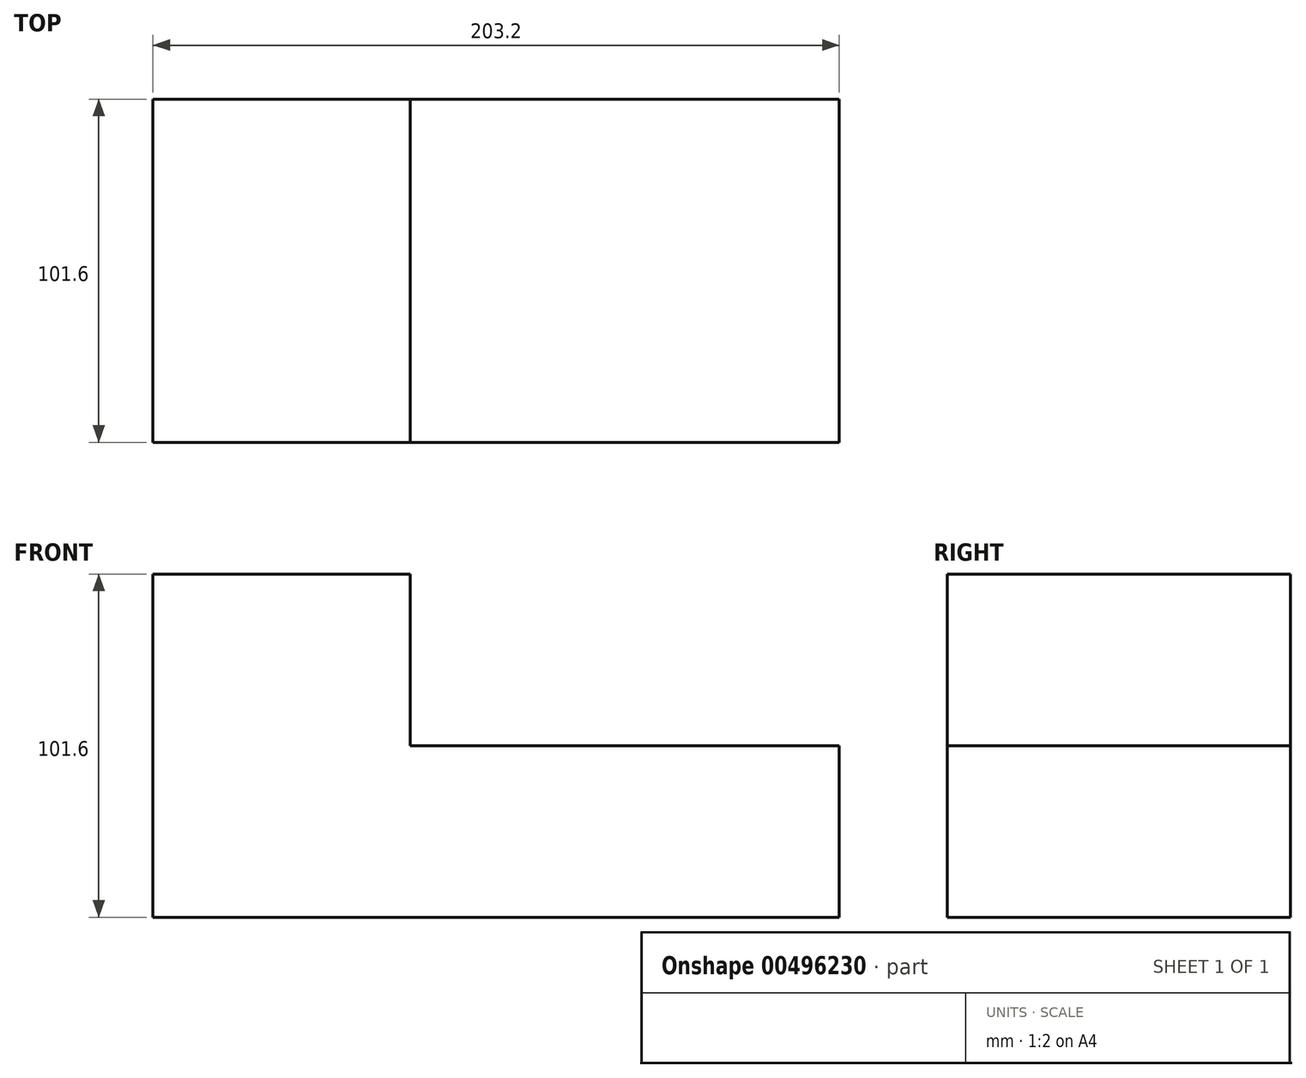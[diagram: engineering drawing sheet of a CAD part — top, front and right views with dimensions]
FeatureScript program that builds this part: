
annotation { "Feature Type Name" : "Feature", "Feature Type Description" : "" }
export const myFeature = defineFeature(function(context is Context, id is Id, definition is map)
    precondition{}
    {
        {
            var Q0;
            Q0=qCreatedBy(makeId("Front.planeOp"),FACE);
            var sketch = newSketch(context, id + "F0", { "sketchPlane" : qUnion([Q0])});
            skLineSegment(sketch, "E0.bottom", {"start": v(0, 0) * mm, "end": v(203.2, 0) * mm});
            skLineSegment(sketch, "E0.top", {"start": v(0, 101.6) * mm, "end": v(203.2, 101.6) * mm});
            skLineSegment(sketch, "E0.left", {"start": v(0, 0) * mm, "end": v(0, 101.6) * mm});
            skLineSegment(sketch, "E0.right", {"start": v(203.2, 0) * mm, "end": v(203.2, 101.6) * mm});
            skLineSegment(sketch, "E1.bottom", {"start": v(203.2, 101.6) * mm, "end": v(76.2, 101.6) * mm});
            skLineSegment(sketch, "E1.top", {"start": v(203.2, 50.8) * mm, "end": v(76.2, 50.8) * mm});
            skLineSegment(sketch, "E1.left", {"start": v(203.2, 101.6) * mm, "end": v(203.2, 50.8) * mm});
            skLineSegment(sketch, "E1.right", {"start": v(76.2, 101.6) * mm, "end": v(76.2, 50.8) * mm});
            skSolve(sketch);
        }
        {
            var Q0;
            Q0=makeQuery(id+"F0.imprint","IMPRINT",FACE,{"disambiguationData":[TD([[makeQuery(id+"F0.imprint","IMPRINT",EDGE,{"derivedFrom":sQuery(id+"F0.wireOp",EDGE,"E0.bottom")}),1.0]])]});
            extrude(context, id + "F1", {"entities" : qUnion([Q0]), "depth" : 101.6 * mm});
        }
    });
